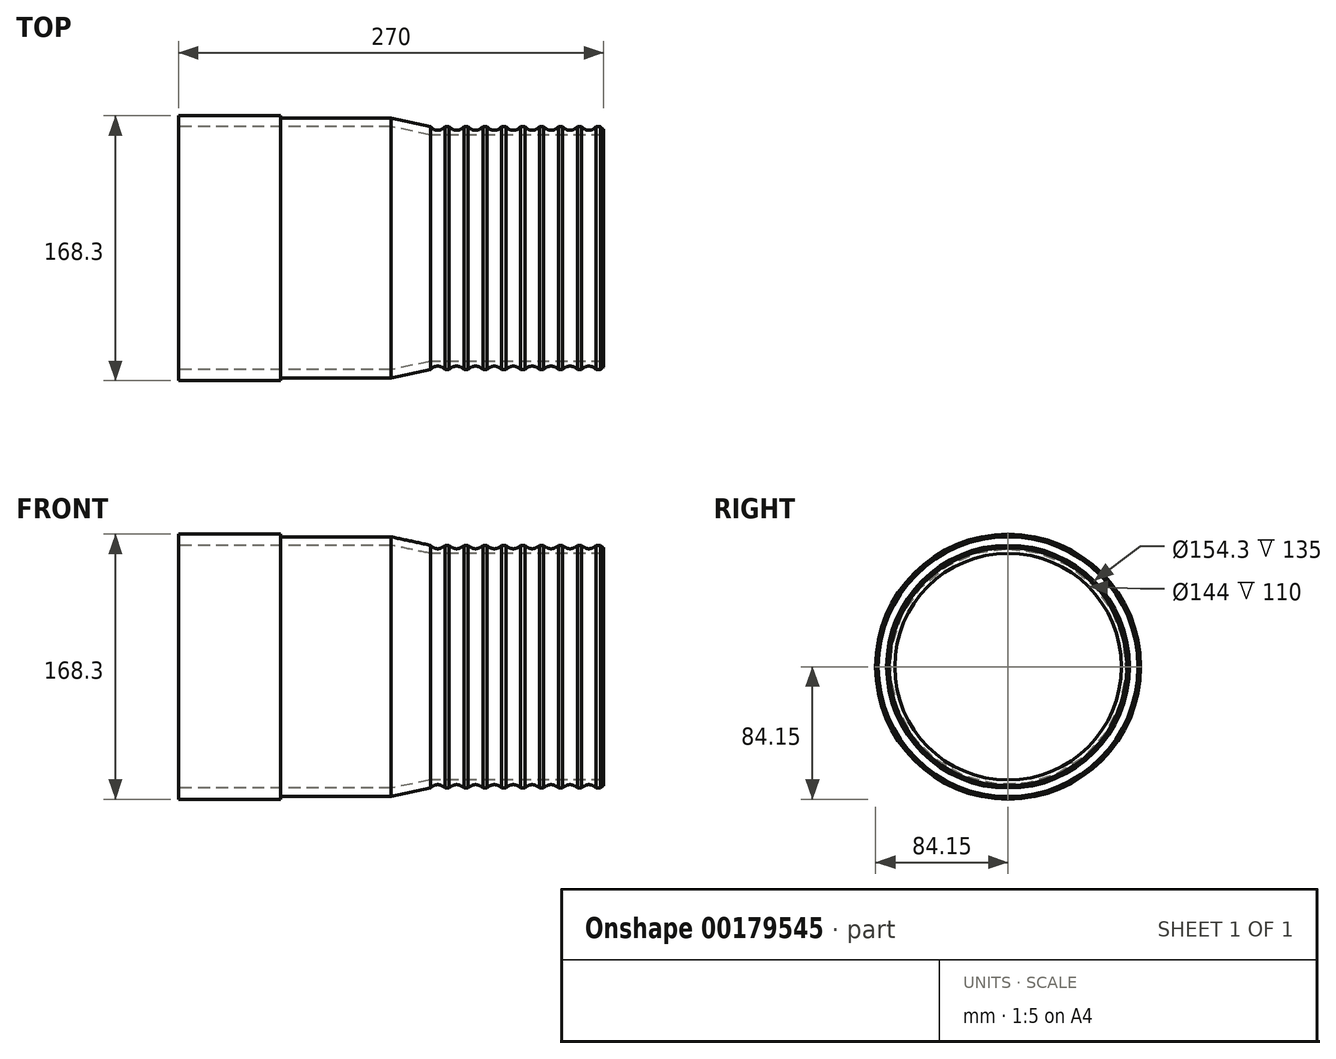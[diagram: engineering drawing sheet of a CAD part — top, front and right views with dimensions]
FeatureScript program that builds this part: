
annotation { "Feature Type Name" : "Feature", "Feature Type Description" : "" }
export const myFeature = defineFeature(function(context is Context, id is Id, definition is map)
    precondition{}
    {
        {
            var Q0;
            Q0=qCreatedBy(makeId("Front.planeOp"),FACE);
            var sketch = newSketch(context, id + "F0", { "sketchPlane" : qUnion([Q0])});
            skLineSegment(sketch, "E0", {"start": v(0, 0) * mm, "end": v(135, 0) * mm});
            skLineSegment(sketch, "E1", {"start": v(135, 0) * mm, "end": v(160, -5.15) * mm});
            skLineSegment(sketch, "E2", {"start": v(160, -5.15) * mm, "end": v(270, -5.15) * mm});
            skLineSegment(sketch, "E3", {"start": v(0, 0) * mm, "end": v(0, 7) * mm});
            skLineSegment(sketch, "E4", {"start": v(0, 7) * mm, "end": v(65, 7) * mm});
            skLineSegment(sketch, "E5", {"start": v(65, 7) * mm, "end": v(65, 5.35) * mm});
            skLineSegment(sketch, "E6", {"start": v(65, 5.35) * mm, "end": v(135, 5.35) * mm});
            skLineSegment(sketch, "E7", {"start": v(135, 5.35) * mm, "end": v(160, 0) * mm, "construction": true});
            skLineSegment(sketch, "E8", {"start": v(160, -20.32) * mm, "end": v(160, 17.36) * mm, "construction": true});
            skLineSegment(sketch, "E9", {"start": v(270, -5.15) * mm, "end": v(270, 59.01) * mm, "construction": true});
            skLineSegment(sketch, "E10", {"start": v(270, -0.24) * mm, "end": v(270, -5.15) * mm});
            skArc(sketch, "E11", {"start": v(160, 0) * mm, "mid": v(164.68, -2.25) * mm, "end": v(169.37, 0) * mm});
            skPoint(sketch, "E12.endSnap0", {"position": v(164.68, -2.25) * mm});
            skArc(sketch, "E13.1.0.0", {"start": v(172, 0) * mm, "mid": v(176.68, -2.25) * mm, "end": v(181.37, 0) * mm});
            skArc(sketch, "E13.2.0.0", {"start": v(184, 0) * mm, "mid": v(188.68, -2.25) * mm, "end": v(193.37, 0) * mm});
            skArc(sketch, "E13.3.0.0", {"start": v(196, 0) * mm, "mid": v(200.68, -2.25) * mm, "end": v(205.37, 0) * mm});
            skArc(sketch, "E13.4.0.0", {"start": v(208, 0) * mm, "mid": v(212.68, -2.25) * mm, "end": v(217.37, 0) * mm});
            skArc(sketch, "E13.5.0.0", {"start": v(220, 0) * mm, "mid": v(224.68, -2.25) * mm, "end": v(229.37, 0) * mm});
            skArc(sketch, "E13.6.0.0", {"start": v(232, 0) * mm, "mid": v(236.68, -2.25) * mm, "end": v(241.37, 0) * mm});
            skArc(sketch, "E13.7.0.0", {"start": v(244, 0) * mm, "mid": v(248.68, -2.25) * mm, "end": v(253.37, 0) * mm});
            skArc(sketch, "E13.8.0.0", {"start": v(256, 0) * mm, "mid": v(260.68, -2.25) * mm, "end": v(265.37, 0) * mm});
            skLineSegment(sketch, "E14", {"start": v(169.37, 0) * mm, "end": v(172, 0) * mm});
            skLineSegment(sketch, "E15.1.0.0", {"start": v(181.37, 0) * mm, "end": v(184, 0) * mm});
            skLineSegment(sketch, "E15.2.0.0", {"start": v(193.37, 0) * mm, "end": v(196, 0) * mm});
            skLineSegment(sketch, "E15.3.0.0", {"start": v(205.37, 0) * mm, "end": v(208, 0) * mm});
            skLineSegment(sketch, "E15.4.0.0", {"start": v(217.37, 0) * mm, "end": v(220, 0) * mm});
            skLineSegment(sketch, "E15.5.0.0", {"start": v(229.37, 0) * mm, "end": v(232, 0) * mm});
            skLineSegment(sketch, "E15.6.0.0", {"start": v(241.37, 0) * mm, "end": v(244, 0) * mm});
            skLineSegment(sketch, "E15.7.0.0", {"start": v(253.37, 0) * mm, "end": v(256, 0) * mm});
            skLineSegment(sketch, "E15.8.0.0", {"start": v(265.37, 0) * mm, "end": v(268, 0) * mm});
            skLineSegment(sketch, "E16", {"start": v(135, 0) * mm, "end": v(135, 19.01) * mm, "construction": true});
            skLineSegment(sketch, "E17", {"start": v(135, 5.35) * mm, "end": v(160, 0) * mm});
            skLineSegment(sketch, "E18", {"start": v(-11.74, -77.15) * mm, "end": v(291.26, -77.15) * mm, "construction": true});
            skArc(sketch, "E19.1.0.0", {"start": v(268, 0) * mm, "mid": v(268.91, -0.92) * mm, "end": v(270, -1.62) * mm});
            skPoint(sketch, "E20.orphan", {"position": v(277.37, 0) * mm});
            skSolve(sketch);
        }
        {
            var Q0;
            Q0=makeQuery(id+"F0.imprint","IMPRINT",FACE,{"disambiguationData":[TD([[makeQuery(id+"F0.imprint","IMPRINT",EDGE,{"derivedFrom":sQuery(id+"F0.wireOp",EDGE,"E0")}),1.0]])]});
            var Q1;
            Q1=sQuery(id+"F0.wireOp",EDGE,"E18");
            revolve(context, id + "F1", {"entities" : qUnion([Q0]), "axis" : qUnion([Q1]), "revolveType" : RevolveType.FULL});
        }
    });
